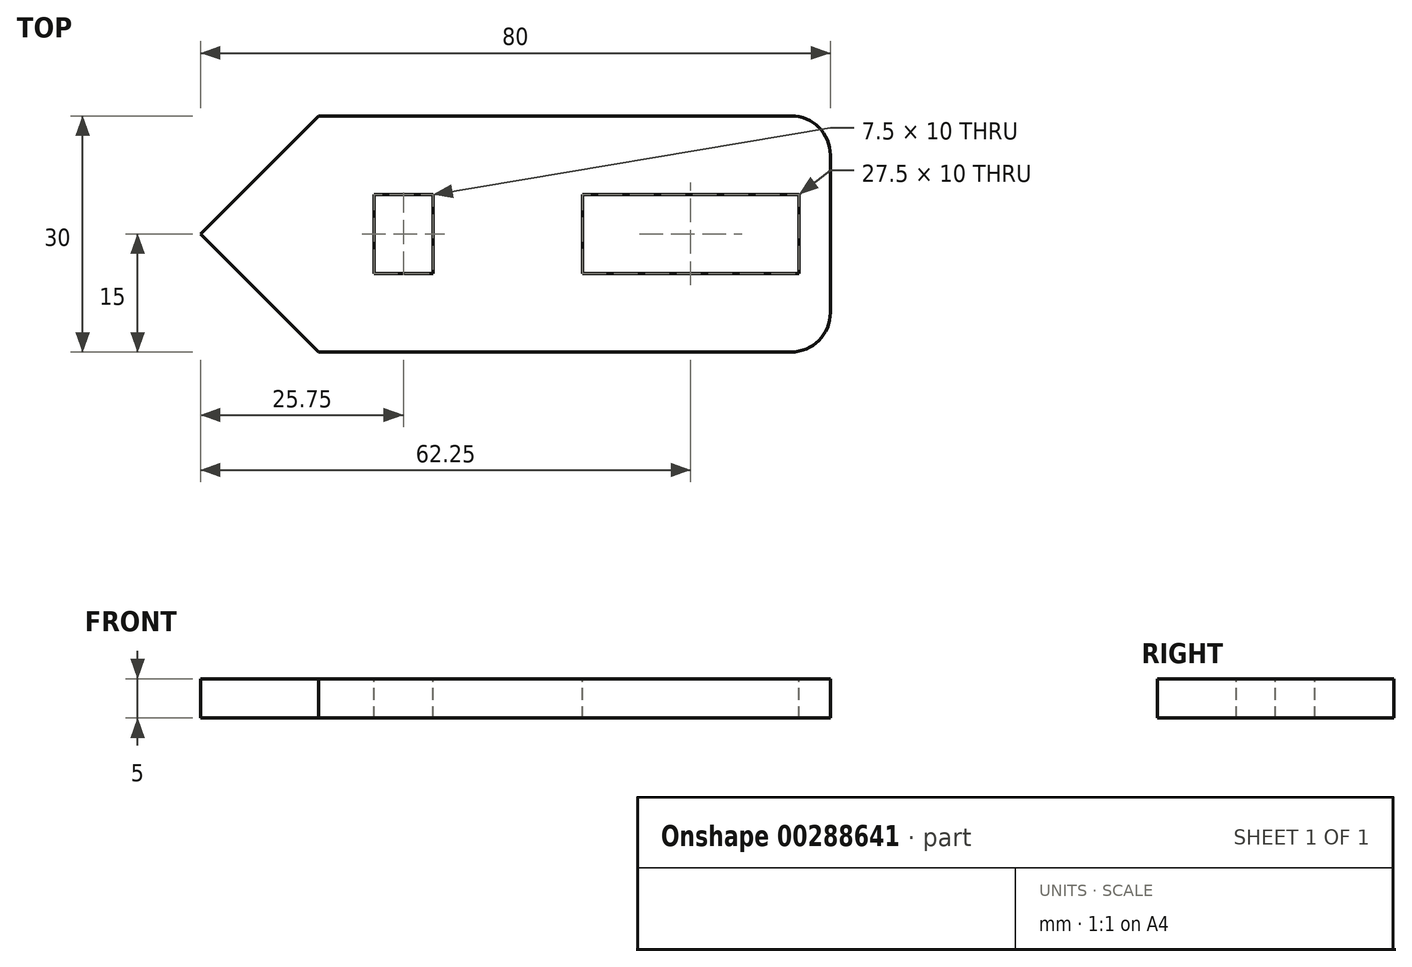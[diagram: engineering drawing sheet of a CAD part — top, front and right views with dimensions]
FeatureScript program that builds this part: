
annotation { "Feature Type Name" : "Feature", "Feature Type Description" : "" }
export const myFeature = defineFeature(function(context is Context, id is Id, definition is map)
    precondition{}
    {
        {
            var Q0;
            Q0=qCreatedBy(makeId("Top.planeOp"),FACE);
            var sketch = newSketch(context, id + "F0", { "sketchPlane" : qUnion([Q0])});
            skLineSegment(sketch, "E0.bottom", {"start": v(43.5, -15) * mm, "end": v(-36.5, -15) * mm});
            skLineSegment(sketch, "E0.top", {"start": v(43.5, 15) * mm, "end": v(-36.5, 15) * mm});
            skLineSegment(sketch, "E0.left", {"start": v(43.5, -15) * mm, "end": v(43.5, 15) * mm});
            skLineSegment(sketch, "E0.right", {"start": v(-36.5, -15) * mm, "end": v(-36.5, 15) * mm});
            skPoint(sketch, "E0.middle", {"position": v(3.5, 0) * mm});
            skSolve(sketch);
        }
        {
            var Q0;
            Q0=makeQuery(id+"F0.imprint","IMPRINT",FACE,{"disambiguationData":[TD([[makeQuery(id+"F0.imprint","IMPRINT",EDGE,{"derivedFrom":sQuery(id+"F0.wireOp",EDGE,"E0.bottom")}),-1.0]])]});
            extrude(context, id + "F1", {"entities" : qUnion([Q0]), "depth" : 5 * mm, "offsetDistance" : 25 * mm});
        }
        {
            var Q0;
            Q0=makeQuery(id+"F1.opExtrude","CAP_FACE",FACE,{"disambiguationData":[OSD([sQuery(id+"F0.wireOp",EDGE,"E0.bottom"),sQuery(id+"F0.wireOp",EDGE,"E0.top"),sQuery(id+"F0.wireOp",EDGE,"E0.left"),sQuery(id+"F0.wireOp",EDGE,"E0.right")])],"isStart":false});
            var sketch = newSketch(context, id + "F2", { "sketchPlane" : qUnion([Q0])});
            skLineSegment(sketch, "E1.bottom", {"start": v(-14.5, 5) * mm, "end": v(-7, 5) * mm});
            skLineSegment(sketch, "E1.top", {"start": v(-14.5, -5) * mm, "end": v(-7, -5) * mm});
            skLineSegment(sketch, "E1.left", {"start": v(-14.5, 5) * mm, "end": v(-14.5, -5) * mm});
            skLineSegment(sketch, "E1.right", {"start": v(-7, 5) * mm, "end": v(-7, -5) * mm});
            skSolve(sketch);
        }
        {
            var Q0;
            Q0=makeQuery(id+"F2.imprint","IMPRINT",FACE,{"disambiguationData":[TD([[makeQuery(id+"F2.imprint","IMPRINT",EDGE,{"derivedFrom":sQuery(id+"F2.wireOp",EDGE,"E1.bottom")}),-1.0]])]});
            extrude(context, id + "F3", {"entities" : qUnion([Q0]), "operationType" : NewBodyOperationType.REMOVE, "oppositeDirection" : true, "depth" : 25 * mm, "offsetDistance" : 25 * mm});
        }
        {
            var Q0;
            Q0=makeQuery(id+"F1.opExtrude","CAP_FACE",FACE,{"disambiguationData":[OSD([sQuery(id+"F0.wireOp",EDGE,"E0.bottom"),sQuery(id+"F0.wireOp",EDGE,"E0.top"),sQuery(id+"F0.wireOp",EDGE,"E0.left"),sQuery(id+"F0.wireOp",EDGE,"E0.right")])],"isStart":false});
            var sketch = newSketch(context, id + "F4", { "sketchPlane" : qUnion([Q0])});
            skLineSegment(sketch, "E2.bottom", {"start": v(12, -5) * mm, "end": v(39.5, -5) * mm});
            skLineSegment(sketch, "E2.top", {"start": v(12, 5) * mm, "end": v(39.5, 5) * mm});
            skLineSegment(sketch, "E2.left", {"start": v(12, -5) * mm, "end": v(12, 5) * mm});
            skLineSegment(sketch, "E2.right", {"start": v(39.5, -5) * mm, "end": v(39.5, 5) * mm});
            skSolve(sketch);
        }
        {
            var Q0;
            Q0 = qSketchRegion(id + "F4", true);
            extrude(context, id + "F5", {"entities" : qUnion([Q0]), "operationType" : NewBodyOperationType.REMOVE, "oppositeDirection" : true, "depth" : 5 * mm, "offsetDistance" : 25 * mm});
        }
        {
            var Q0;
            Q0=makeQuery(id+"F1.opExtrude","SWEPT_EDGE",EDGE,{"disambiguationData":[OSD([sQuery(id+"F0.wireOp",EDGE,"E0.bottom"),sQuery(id+"F0.wireOp",EDGE,"E0.right")])]});
            var Q1;
            Q1=makeQuery(id+"F1.opExtrude","SWEPT_EDGE",EDGE,{"disambiguationData":[OSD([sQuery(id+"F0.wireOp",EDGE,"E0.top"),sQuery(id+"F0.wireOp",EDGE,"E0.right")])]});
            chamfer(context, id + "F6", {"entities" : qUnion([Q0, Q1]), "width" : 15 * mm, "tangentPropagation" : true});
        }
        {
            var Q0;
            Q0=makeQuery(id+"F1.opExtrude","SWEPT_EDGE",EDGE,{"disambiguationData":[OSD([sQuery(id+"F0.wireOp",EDGE,"E0.bottom"),sQuery(id+"F0.wireOp",EDGE,"E0.left")])]});
            var Q1;
            Q1=makeQuery(id+"F1.opExtrude","SWEPT_EDGE",EDGE,{"disambiguationData":[OSD([sQuery(id+"F0.wireOp",EDGE,"E0.top"),sQuery(id+"F0.wireOp",EDGE,"E0.left")])]});
            fillet(context, id + "F7", {"entities" : qUnion([Q0, Q1]), "radius" : 5 * mm, "tangentPropagation" : true, "allowEdgeOverflow" : false});
        }
    });
